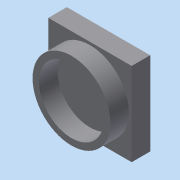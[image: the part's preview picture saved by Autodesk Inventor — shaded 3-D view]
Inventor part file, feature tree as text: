
AUTODESK INVENTOR PART (.ipt)
format: ipt  version: 2019.4 (Build 234330000, 330)  size: 105,472 bytes
history: native  units: mm
features: extrude x2, sketch x2, projected_geometry x1
ambient origin geometry x8: Origin, YZ Plane, XZ Plane, XY Plane, X Axis, Y Axis, Z Axis, Center Point
bodies: Solid1 (feature_tree)
feature tree (5):
  extrude  "Extrusion1"  Depth=9.0mm
  extrude  "Extrusion2"  Depth=2.0mm
  sketch  "Sketch1"  dims[d0=9.0mm d1=9.0mm]
  sketch  "Sketch2"  dims[d2=2.0mm d3=0.0mm d4=8.4mm d5=7.0mm d6=2.0mm d7=0.0mm]
  projected_geometry  "Projected Loop1"
